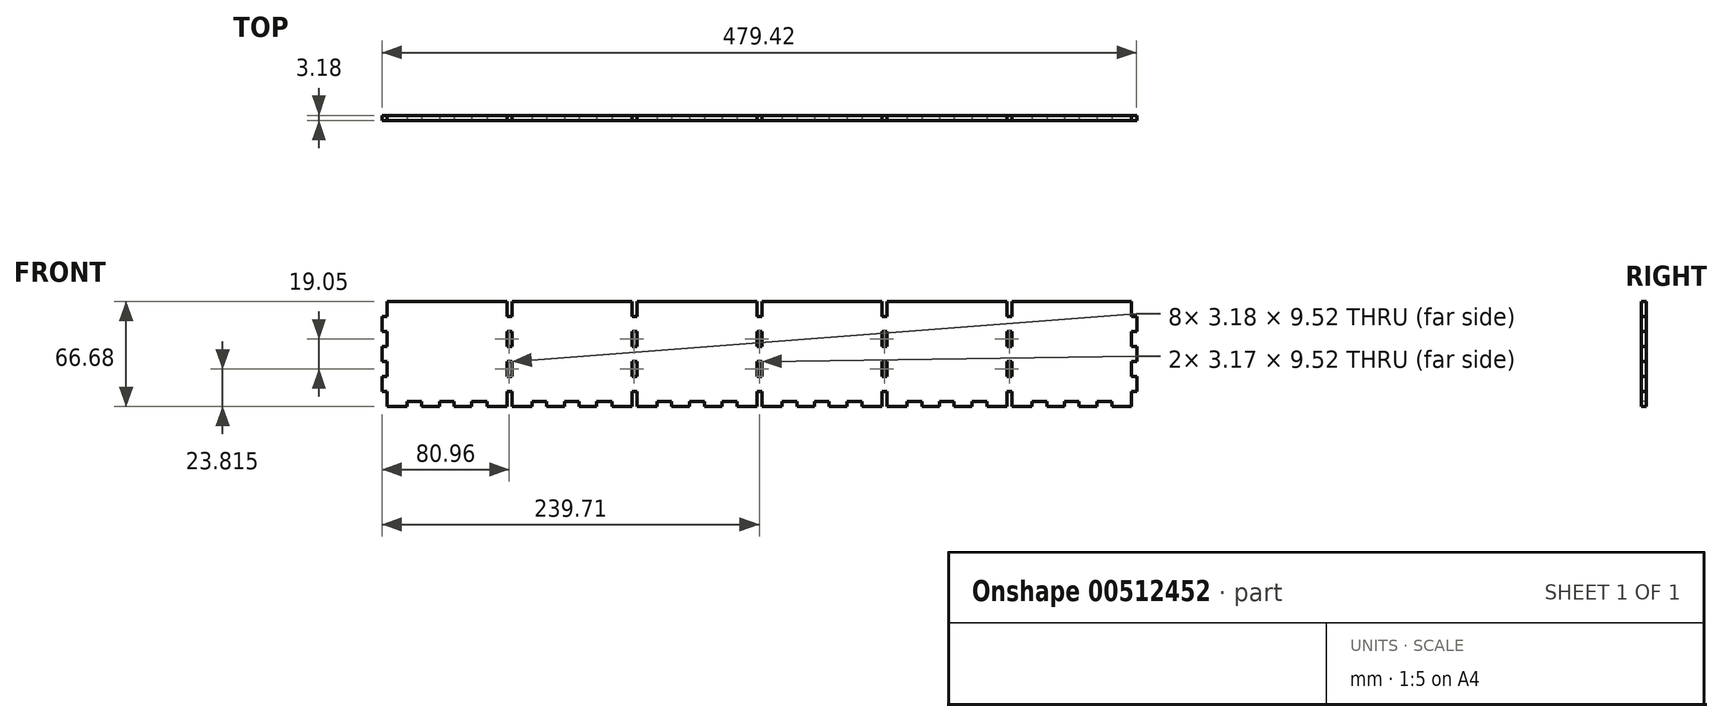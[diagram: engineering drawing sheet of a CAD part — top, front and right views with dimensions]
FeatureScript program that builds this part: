
annotation { "Feature Type Name" : "Feature", "Feature Type Description" : "" }
export const myFeature = defineFeature(function(context is Context, id is Id, definition is map)
    precondition{}
    {
        {
            var Q0;
            Q0=qCreatedBy(makeId("Front.planeOp"),FACE);
            var sketch = newSketch(context, id + "F0", { "sketchPlane" : qUnion([Q0])});
            skLineSegment(sketch, "E0.bottom", {"start": v(-239.71, 33.34) * mm, "end": v(239.71, 33.34) * mm});
            skLineSegment(sketch, "E0.top", {"start": v(-239.71, -33.34) * mm, "end": v(239.71, -33.34) * mm});
            skLineSegment(sketch, "E0.left", {"start": v(-239.71, 33.34) * mm, "end": v(-239.71, -33.34) * mm});
            skLineSegment(sketch, "E0.right", {"start": v(239.71, 33.34) * mm, "end": v(239.71, -33.34) * mm});
            skSolve(sketch);
        }
        {
            var Q0;
            Q0=makeQuery(id+"F0.imprint","IMPRINT",FACE,{"disambiguationData":[TD([[makeQuery(id+"F0.imprint","IMPRINT",EDGE,{"derivedFrom":sQuery(id+"F0.wireOp",EDGE,"E0.bottom")}),-1.0]])]});
            extrude(context, id + "F1", {"entities" : qUnion([Q0]), "depth" : 3.17 * mm});
        }
        {
            var Q0;
            Q0=makeQuery(id+"F1.opExtrude","CAP_FACE",FACE,{"disambiguationData":[OSD([sQuery(id+"F0.wireOp",EDGE,"E0.bottom"),sQuery(id+"F0.wireOp",EDGE,"E0.top"),sQuery(id+"F0.wireOp",EDGE,"E0.left"),sQuery(id+"F0.wireOp",EDGE,"E0.right")])],"isStart":false});
            var sketch = newSketch(context, id + "F2", { "sketchPlane" : qUnion([Q0])});
            skLineSegment(sketch, "E1.bottom", {"start": v(-239.71, -33.34) * mm, "end": v(-236.54, -33.34) * mm});
            skLineSegment(sketch, "E1.top", {"start": v(-239.71, -23.81) * mm, "end": v(-236.54, -23.81) * mm});
            skLineSegment(sketch, "E1.left", {"start": v(-239.71, -33.34) * mm, "end": v(-239.71, -23.81) * mm});
            skLineSegment(sketch, "E1.right", {"start": v(-236.54, -33.34) * mm, "end": v(-236.54, -23.81) * mm});
            skLineSegment(sketch, "E2.0.1.0", {"start": v(-236.54, -14.29) * mm, "end": v(-236.54, -4.76) * mm});
            skLineSegment(sketch, "E2.0.1.1", {"start": v(-239.71, -14.29) * mm, "end": v(-239.71, -4.76) * mm});
            skLineSegment(sketch, "E2.0.1.2", {"start": v(-239.71, -4.76) * mm, "end": v(-236.54, -4.76) * mm});
            skLineSegment(sketch, "E2.0.1.3", {"start": v(-239.71, -14.29) * mm, "end": v(-236.54, -14.29) * mm});
            skLineSegment(sketch, "E2.0.2.0", {"start": v(-236.54, 4.76) * mm, "end": v(-236.54, 14.29) * mm});
            skLineSegment(sketch, "E2.0.2.1", {"start": v(-239.71, 4.76) * mm, "end": v(-239.71, 14.29) * mm});
            skLineSegment(sketch, "E2.0.2.2", {"start": v(-239.71, 14.29) * mm, "end": v(-236.54, 14.29) * mm});
            skLineSegment(sketch, "E2.0.2.3", {"start": v(-239.71, 4.76) * mm, "end": v(-236.54, 4.76) * mm});
            skLineSegment(sketch, "E2.0.3.0", {"start": v(-236.54, 23.81) * mm, "end": v(-236.54, 33.34) * mm});
            skLineSegment(sketch, "E2.0.3.1", {"start": v(-239.71, 23.81) * mm, "end": v(-239.71, 33.34) * mm});
            skLineSegment(sketch, "E2.0.3.2", {"start": v(-239.71, 33.34) * mm, "end": v(-236.54, 33.34) * mm});
            skLineSegment(sketch, "E2.0.3.3", {"start": v(-239.71, 23.81) * mm, "end": v(-236.54, 23.81) * mm});
            skLineSegment(sketch, "E2.1.0.0", {"start": v(-157.16, -33.34) * mm, "end": v(-157.16, -23.81) * mm});
            skLineSegment(sketch, "E2.1.0.1", {"start": v(-160.34, -33.34) * mm, "end": v(-160.34, -23.81) * mm});
            skLineSegment(sketch, "E2.1.0.2", {"start": v(-160.34, -23.81) * mm, "end": v(-157.16, -23.81) * mm});
            skLineSegment(sketch, "E2.1.0.3", {"start": v(-160.34, -33.34) * mm, "end": v(-157.16, -33.34) * mm});
            skLineSegment(sketch, "E2.1.1.0", {"start": v(-157.16, -14.29) * mm, "end": v(-157.16, -4.76) * mm});
            skLineSegment(sketch, "E2.1.1.1", {"start": v(-160.34, -14.29) * mm, "end": v(-160.34, -4.76) * mm});
            skLineSegment(sketch, "E2.1.1.2", {"start": v(-160.34, -4.76) * mm, "end": v(-157.16, -4.76) * mm});
            skLineSegment(sketch, "E2.1.1.3", {"start": v(-160.34, -14.29) * mm, "end": v(-157.16, -14.29) * mm});
            skLineSegment(sketch, "E2.1.2.0", {"start": v(-157.16, 4.76) * mm, "end": v(-157.16, 14.29) * mm});
            skLineSegment(sketch, "E2.1.2.1", {"start": v(-160.34, 4.76) * mm, "end": v(-160.34, 14.29) * mm});
            skLineSegment(sketch, "E2.1.2.2", {"start": v(-160.34, 14.29) * mm, "end": v(-157.16, 14.29) * mm});
            skLineSegment(sketch, "E2.1.2.3", {"start": v(-160.34, 4.76) * mm, "end": v(-157.16, 4.76) * mm});
            skLineSegment(sketch, "E2.1.3.0", {"start": v(-157.16, 23.81) * mm, "end": v(-157.16, 33.34) * mm});
            skLineSegment(sketch, "E2.1.3.1", {"start": v(-160.34, 23.81) * mm, "end": v(-160.34, 33.34) * mm});
            skLineSegment(sketch, "E2.1.3.2", {"start": v(-160.34, 33.34) * mm, "end": v(-157.16, 33.34) * mm});
            skLineSegment(sketch, "E2.1.3.3", {"start": v(-160.34, 23.81) * mm, "end": v(-157.16, 23.81) * mm});
            skLineSegment(sketch, "E2.2.0.0", {"start": v(-77.79, -33.34) * mm, "end": v(-77.79, -23.81) * mm});
            skLineSegment(sketch, "E2.2.0.1", {"start": v(-80.96, -33.34) * mm, "end": v(-80.96, -23.81) * mm});
            skLineSegment(sketch, "E2.2.0.2", {"start": v(-80.96, -23.81) * mm, "end": v(-77.79, -23.81) * mm});
            skLineSegment(sketch, "E2.2.0.3", {"start": v(-80.96, -33.34) * mm, "end": v(-77.79, -33.34) * mm});
            skLineSegment(sketch, "E2.2.1.0", {"start": v(-77.79, -14.29) * mm, "end": v(-77.79, -4.76) * mm});
            skLineSegment(sketch, "E2.2.1.1", {"start": v(-80.96, -14.29) * mm, "end": v(-80.96, -4.76) * mm});
            skLineSegment(sketch, "E2.2.1.2", {"start": v(-80.96, -4.76) * mm, "end": v(-77.79, -4.76) * mm});
            skLineSegment(sketch, "E2.2.1.3", {"start": v(-80.96, -14.29) * mm, "end": v(-77.79, -14.29) * mm});
            skLineSegment(sketch, "E2.2.2.0", {"start": v(-77.79, 4.76) * mm, "end": v(-77.79, 14.29) * mm});
            skLineSegment(sketch, "E2.2.2.1", {"start": v(-80.96, 4.76) * mm, "end": v(-80.96, 14.29) * mm});
            skLineSegment(sketch, "E2.2.2.2", {"start": v(-80.96, 14.29) * mm, "end": v(-77.79, 14.29) * mm});
            skLineSegment(sketch, "E2.2.2.3", {"start": v(-80.96, 4.76) * mm, "end": v(-77.79, 4.76) * mm});
            skLineSegment(sketch, "E2.2.3.0", {"start": v(-77.79, 23.81) * mm, "end": v(-77.79, 33.34) * mm});
            skLineSegment(sketch, "E2.2.3.1", {"start": v(-80.96, 23.81) * mm, "end": v(-80.96, 33.34) * mm});
            skLineSegment(sketch, "E2.2.3.2", {"start": v(-80.96, 33.34) * mm, "end": v(-77.79, 33.34) * mm});
            skLineSegment(sketch, "E2.2.3.3", {"start": v(-80.96, 23.81) * mm, "end": v(-77.79, 23.81) * mm});
            skLineSegment(sketch, "E2.direction1", {"start": v(-239.71, -33.34) * mm, "end": v(-160.34, -33.34) * mm, "construction": true});
            skLineSegment(sketch, "E2.direction2", {"start": v(-239.71, -33.34) * mm, "end": v(-239.71, -14.29) * mm, "construction": true});
            skLineSegment(sketch, "E3.0.3.0", {"start": v(1.59, -33.34) * mm, "end": v(1.59, -23.81) * mm});
            skLineSegment(sketch, "E3.3.3.0", {"start": v(-1.59, -33.34) * mm, "end": v(-1.59, -23.81) * mm});
            skLineSegment(sketch, "E3.6.3.0", {"start": v(-1.59, -23.81) * mm, "end": v(1.59, -23.81) * mm});
            skLineSegment(sketch, "E3.9.3.0", {"start": v(-1.59, -33.34) * mm, "end": v(1.59, -33.34) * mm});
            skLineSegment(sketch, "E3.0.3.1", {"start": v(1.59, -14.29) * mm, "end": v(1.59, -4.76) * mm});
            skLineSegment(sketch, "E3.3.3.1", {"start": v(-1.59, -14.29) * mm, "end": v(-1.59, -4.76) * mm});
            skLineSegment(sketch, "E3.6.3.1", {"start": v(-1.59, -4.76) * mm, "end": v(1.59, -4.76) * mm});
            skLineSegment(sketch, "E3.9.3.1", {"start": v(-1.59, -14.29) * mm, "end": v(1.59, -14.29) * mm});
            skLineSegment(sketch, "E3.0.3.2", {"start": v(1.59, 4.76) * mm, "end": v(1.59, 14.29) * mm});
            skLineSegment(sketch, "E3.3.3.2", {"start": v(-1.59, 4.76) * mm, "end": v(-1.59, 14.29) * mm});
            skLineSegment(sketch, "E3.6.3.2", {"start": v(-1.59, 14.29) * mm, "end": v(1.59, 14.29) * mm});
            skLineSegment(sketch, "E3.9.3.2", {"start": v(-1.59, 4.76) * mm, "end": v(1.59, 4.76) * mm});
            skLineSegment(sketch, "E3.0.3.3", {"start": v(1.59, 23.81) * mm, "end": v(1.59, 33.34) * mm});
            skLineSegment(sketch, "E3.3.3.3", {"start": v(-1.59, 23.81) * mm, "end": v(-1.59, 33.34) * mm});
            skLineSegment(sketch, "E3.6.3.3", {"start": v(-1.59, 33.34) * mm, "end": v(1.59, 33.34) * mm});
            skLineSegment(sketch, "E3.9.3.3", {"start": v(-1.59, 23.81) * mm, "end": v(1.59, 23.81) * mm});
            skLineSegment(sketch, "E3.0.4.0", {"start": v(80.96, -33.34) * mm, "end": v(80.96, -23.81) * mm});
            skLineSegment(sketch, "E3.3.4.0", {"start": v(77.79, -33.34) * mm, "end": v(77.79, -23.81) * mm});
            skLineSegment(sketch, "E3.6.4.0", {"start": v(77.79, -23.81) * mm, "end": v(80.96, -23.81) * mm});
            skLineSegment(sketch, "E3.9.4.0", {"start": v(77.79, -33.34) * mm, "end": v(80.96, -33.34) * mm});
            skLineSegment(sketch, "E3.0.4.1", {"start": v(80.96, -14.29) * mm, "end": v(80.96, -4.76) * mm});
            skLineSegment(sketch, "E3.3.4.1", {"start": v(77.79, -14.29) * mm, "end": v(77.79, -4.76) * mm});
            skLineSegment(sketch, "E3.6.4.1", {"start": v(77.79, -4.76) * mm, "end": v(80.96, -4.76) * mm});
            skLineSegment(sketch, "E3.9.4.1", {"start": v(77.79, -14.29) * mm, "end": v(80.96, -14.29) * mm});
            skLineSegment(sketch, "E3.0.4.2", {"start": v(80.96, 4.76) * mm, "end": v(80.96, 14.29) * mm});
            skLineSegment(sketch, "E3.3.4.2", {"start": v(77.79, 4.76) * mm, "end": v(77.79, 14.29) * mm});
            skLineSegment(sketch, "E3.6.4.2", {"start": v(77.79, 14.29) * mm, "end": v(80.96, 14.29) * mm});
            skLineSegment(sketch, "E3.9.4.2", {"start": v(77.79, 4.76) * mm, "end": v(80.96, 4.76) * mm});
            skLineSegment(sketch, "E3.0.4.3", {"start": v(80.96, 23.81) * mm, "end": v(80.96, 33.34) * mm});
            skLineSegment(sketch, "E3.3.4.3", {"start": v(77.79, 23.81) * mm, "end": v(77.79, 33.34) * mm});
            skLineSegment(sketch, "E3.6.4.3", {"start": v(77.79, 33.34) * mm, "end": v(80.96, 33.34) * mm});
            skLineSegment(sketch, "E3.9.4.3", {"start": v(77.79, 23.81) * mm, "end": v(80.96, 23.81) * mm});
            skLineSegment(sketch, "E3.0.5.0", {"start": v(160.34, -33.34) * mm, "end": v(160.34, -23.81) * mm});
            skLineSegment(sketch, "E3.3.5.0", {"start": v(157.16, -33.34) * mm, "end": v(157.16, -23.81) * mm});
            skLineSegment(sketch, "E3.6.5.0", {"start": v(157.16, -23.81) * mm, "end": v(160.34, -23.81) * mm});
            skLineSegment(sketch, "E3.9.5.0", {"start": v(157.16, -33.34) * mm, "end": v(160.34, -33.34) * mm});
            skLineSegment(sketch, "E3.0.5.1", {"start": v(160.34, -14.29) * mm, "end": v(160.34, -4.76) * mm});
            skLineSegment(sketch, "E3.3.5.1", {"start": v(157.16, -14.29) * mm, "end": v(157.16, -4.76) * mm});
            skLineSegment(sketch, "E3.6.5.1", {"start": v(157.16, -4.76) * mm, "end": v(160.34, -4.76) * mm});
            skLineSegment(sketch, "E3.9.5.1", {"start": v(157.16, -14.29) * mm, "end": v(160.34, -14.29) * mm});
            skLineSegment(sketch, "E3.0.5.2", {"start": v(160.34, 4.76) * mm, "end": v(160.34, 14.29) * mm});
            skLineSegment(sketch, "E3.3.5.2", {"start": v(157.16, 4.76) * mm, "end": v(157.16, 14.29) * mm});
            skLineSegment(sketch, "E3.6.5.2", {"start": v(157.16, 14.29) * mm, "end": v(160.34, 14.29) * mm});
            skLineSegment(sketch, "E3.9.5.2", {"start": v(157.16, 4.76) * mm, "end": v(160.34, 4.76) * mm});
            skLineSegment(sketch, "E3.0.5.3", {"start": v(160.34, 23.81) * mm, "end": v(160.34, 33.34) * mm});
            skLineSegment(sketch, "E3.3.5.3", {"start": v(157.16, 23.81) * mm, "end": v(157.16, 33.34) * mm});
            skLineSegment(sketch, "E3.6.5.3", {"start": v(157.16, 33.34) * mm, "end": v(160.34, 33.34) * mm});
            skLineSegment(sketch, "E3.9.5.3", {"start": v(157.16, 23.81) * mm, "end": v(160.34, 23.81) * mm});
            skLineSegment(sketch, "E3.0.6.0", {"start": v(239.71, -33.34) * mm, "end": v(239.71, -23.81) * mm});
            skLineSegment(sketch, "E3.3.6.0", {"start": v(236.54, -33.34) * mm, "end": v(236.54, -23.81) * mm});
            skLineSegment(sketch, "E3.6.6.0", {"start": v(236.54, -23.81) * mm, "end": v(239.71, -23.81) * mm});
            skLineSegment(sketch, "E3.9.6.0", {"start": v(236.54, -33.34) * mm, "end": v(239.71, -33.34) * mm});
            skLineSegment(sketch, "E3.0.6.1", {"start": v(239.71, -14.29) * mm, "end": v(239.71, -4.76) * mm});
            skLineSegment(sketch, "E3.3.6.1", {"start": v(236.54, -14.29) * mm, "end": v(236.54, -4.76) * mm});
            skLineSegment(sketch, "E3.6.6.1", {"start": v(236.54, -4.76) * mm, "end": v(239.71, -4.76) * mm});
            skLineSegment(sketch, "E3.9.6.1", {"start": v(236.54, -14.29) * mm, "end": v(239.71, -14.29) * mm});
            skLineSegment(sketch, "E3.0.6.2", {"start": v(239.71, 4.76) * mm, "end": v(239.71, 14.29) * mm});
            skLineSegment(sketch, "E3.3.6.2", {"start": v(236.54, 4.76) * mm, "end": v(236.54, 14.29) * mm});
            skLineSegment(sketch, "E3.6.6.2", {"start": v(236.54, 14.29) * mm, "end": v(239.71, 14.29) * mm});
            skLineSegment(sketch, "E3.9.6.2", {"start": v(236.54, 4.76) * mm, "end": v(239.71, 4.76) * mm});
            skLineSegment(sketch, "E3.0.6.3", {"start": v(239.71, 23.81) * mm, "end": v(239.71, 33.34) * mm});
            skLineSegment(sketch, "E3.3.6.3", {"start": v(236.54, 23.81) * mm, "end": v(236.54, 33.34) * mm});
            skLineSegment(sketch, "E3.6.6.3", {"start": v(236.54, 33.34) * mm, "end": v(239.71, 33.34) * mm});
            skLineSegment(sketch, "E3.9.6.3", {"start": v(236.54, 23.81) * mm, "end": v(239.71, 23.81) * mm});
            skSolve(sketch);
        }
        {
            var Q0;
            Q0 = qSketchRegion(id + "F2", true);
            extrude(context, id + "F3", {"entities" : qUnion([Q0]), "operationType" : NewBodyOperationType.REMOVE, "endBound" : BoundingType.THROUGH_ALL, "oppositeDirection" : true, "depth" : 25.4 * mm});
        }
        {
            var Q0;
            Q0=makeQuery(id+"F1.opExtrude","CAP_FACE",FACE,{"disambiguationData":[OSD([sQuery(id+"F0.wireOp",EDGE,"E0.bottom"),sQuery(id+"F0.wireOp",EDGE,"E0.top"),sQuery(id+"F0.wireOp",EDGE,"E0.left"),sQuery(id+"F0.wireOp",EDGE,"E0.right")])],"isStart":false});
            var sketch = newSketch(context, id + "F4", { "sketchPlane" : qUnion([Q0])});
            skLineSegment(sketch, "E4.bottom", {"start": v(-223.84, -33.34) * mm, "end": v(-214.31, -33.34) * mm});
            skLineSegment(sketch, "E4.top", {"start": v(-223.84, -30.16) * mm, "end": v(-214.31, -30.16) * mm});
            skLineSegment(sketch, "E4.left", {"start": v(-223.84, -33.34) * mm, "end": v(-223.84, -30.16) * mm});
            skLineSegment(sketch, "E4.right", {"start": v(-214.31, -33.34) * mm, "end": v(-214.31, -30.16) * mm});
            skLineSegment(sketch, "E5.1.0.0", {"start": v(-193.68, -33.34) * mm, "end": v(-193.68, -30.16) * mm});
            skLineSegment(sketch, "E5.1.0.1", {"start": v(-203.2, -33.34) * mm, "end": v(-203.2, -30.16) * mm});
            skLineSegment(sketch, "E5.1.0.2", {"start": v(-203.2, -30.16) * mm, "end": v(-193.68, -30.16) * mm});
            skLineSegment(sketch, "E5.1.0.3", {"start": v(-203.2, -33.34) * mm, "end": v(-193.68, -33.34) * mm});
            skLineSegment(sketch, "E5.2.0.0", {"start": v(-173.04, -33.34) * mm, "end": v(-173.04, -30.16) * mm});
            skLineSegment(sketch, "E5.2.0.1", {"start": v(-182.56, -33.34) * mm, "end": v(-182.56, -30.16) * mm});
            skLineSegment(sketch, "E5.2.0.2", {"start": v(-182.56, -30.16) * mm, "end": v(-173.04, -30.16) * mm});
            skLineSegment(sketch, "E5.2.0.3", {"start": v(-182.56, -33.34) * mm, "end": v(-173.04, -33.34) * mm});
            skLineSegment(sketch, "E5.direction1", {"start": v(-223.84, -33.34) * mm, "end": v(-203.2, -33.34) * mm, "construction": true});
            skLineSegment(sketch, "E6.1.0.0", {"start": v(-144.46, -30.16) * mm, "end": v(-134.94, -30.16) * mm});
            skLineSegment(sketch, "E6.1.0.1", {"start": v(-144.46, -33.34) * mm, "end": v(-123.83, -33.34) * mm, "construction": true});
            skLineSegment(sketch, "E6.1.0.2", {"start": v(-123.83, -33.34) * mm, "end": v(-114.3, -33.34) * mm});
            skLineSegment(sketch, "E6.1.0.3", {"start": v(-103.19, -33.34) * mm, "end": v(-93.66, -33.34) * mm});
            skLineSegment(sketch, "E6.1.0.4", {"start": v(-123.83, -30.16) * mm, "end": v(-114.3, -30.16) * mm});
            skLineSegment(sketch, "E6.1.0.5", {"start": v(-103.19, -30.16) * mm, "end": v(-93.66, -30.16) * mm});
            skLineSegment(sketch, "E6.1.0.6", {"start": v(-144.46, -33.34) * mm, "end": v(-134.94, -33.34) * mm});
            skLineSegment(sketch, "E6.1.0.7", {"start": v(-134.94, -33.34) * mm, "end": v(-134.94, -30.16) * mm});
            skLineSegment(sketch, "E6.1.0.8", {"start": v(-144.46, -33.34) * mm, "end": v(-144.46, -30.16) * mm});
            skLineSegment(sketch, "E6.1.0.9", {"start": v(-103.19, -33.34) * mm, "end": v(-103.19, -30.16) * mm});
            skLineSegment(sketch, "E6.1.0.10", {"start": v(-123.83, -33.34) * mm, "end": v(-123.83, -30.16) * mm});
            skLineSegment(sketch, "E6.1.0.11", {"start": v(-93.66, -33.34) * mm, "end": v(-93.66, -30.16) * mm});
            skLineSegment(sketch, "E6.1.0.12", {"start": v(-114.3, -33.34) * mm, "end": v(-114.3, -30.16) * mm});
            skLineSegment(sketch, "E6.2.0.0", {"start": v(-65.09, -30.16) * mm, "end": v(-55.56, -30.16) * mm});
            skLineSegment(sketch, "E6.2.0.1", {"start": v(-65.09, -33.34) * mm, "end": v(-44.45, -33.34) * mm, "construction": true});
            skLineSegment(sketch, "E6.2.0.2", {"start": v(-44.45, -33.34) * mm, "end": v(-34.93, -33.34) * mm});
            skLineSegment(sketch, "E6.2.0.3", {"start": v(-23.81, -33.34) * mm, "end": v(-14.29, -33.34) * mm});
            skLineSegment(sketch, "E6.2.0.4", {"start": v(-44.45, -30.16) * mm, "end": v(-34.93, -30.16) * mm});
            skLineSegment(sketch, "E6.2.0.5", {"start": v(-23.81, -30.16) * mm, "end": v(-14.29, -30.16) * mm});
            skLineSegment(sketch, "E6.2.0.6", {"start": v(-65.09, -33.34) * mm, "end": v(-55.56, -33.34) * mm});
            skLineSegment(sketch, "E6.2.0.7", {"start": v(-55.56, -33.34) * mm, "end": v(-55.56, -30.16) * mm});
            skLineSegment(sketch, "E6.2.0.8", {"start": v(-65.09, -33.34) * mm, "end": v(-65.09, -30.16) * mm});
            skLineSegment(sketch, "E6.2.0.9", {"start": v(-23.81, -33.34) * mm, "end": v(-23.81, -30.16) * mm});
            skLineSegment(sketch, "E6.2.0.10", {"start": v(-44.45, -33.34) * mm, "end": v(-44.45, -30.16) * mm});
            skLineSegment(sketch, "E6.2.0.11", {"start": v(-14.29, -33.34) * mm, "end": v(-14.29, -30.16) * mm});
            skLineSegment(sketch, "E6.2.0.12", {"start": v(-34.93, -33.34) * mm, "end": v(-34.93, -30.16) * mm});
            skLineSegment(sketch, "E6.3.0.0", {"start": v(14.29, -30.16) * mm, "end": v(23.81, -30.16) * mm});
            skLineSegment(sketch, "E6.3.0.1", {"start": v(14.29, -33.34) * mm, "end": v(34.92, -33.34) * mm, "construction": true});
            skLineSegment(sketch, "E6.3.0.2", {"start": v(34.92, -33.34) * mm, "end": v(44.45, -33.34) * mm});
            skLineSegment(sketch, "E6.3.0.3", {"start": v(55.56, -33.34) * mm, "end": v(65.09, -33.34) * mm});
            skLineSegment(sketch, "E6.3.0.4", {"start": v(34.92, -30.16) * mm, "end": v(44.45, -30.16) * mm});
            skLineSegment(sketch, "E6.3.0.5", {"start": v(55.56, -30.16) * mm, "end": v(65.09, -30.16) * mm});
            skLineSegment(sketch, "E6.3.0.6", {"start": v(14.29, -33.34) * mm, "end": v(23.81, -33.34) * mm});
            skLineSegment(sketch, "E6.3.0.7", {"start": v(23.81, -33.34) * mm, "end": v(23.81, -30.16) * mm});
            skLineSegment(sketch, "E6.3.0.8", {"start": v(14.29, -33.34) * mm, "end": v(14.29, -30.16) * mm});
            skLineSegment(sketch, "E6.3.0.9", {"start": v(55.56, -33.34) * mm, "end": v(55.56, -30.16) * mm});
            skLineSegment(sketch, "E6.3.0.10", {"start": v(34.92, -33.34) * mm, "end": v(34.92, -30.16) * mm});
            skLineSegment(sketch, "E6.3.0.11", {"start": v(65.09, -33.34) * mm, "end": v(65.09, -30.16) * mm});
            skLineSegment(sketch, "E6.3.0.12", {"start": v(44.45, -33.34) * mm, "end": v(44.45, -30.16) * mm});
            skLineSegment(sketch, "E6.4.0.0", {"start": v(93.66, -30.16) * mm, "end": v(103.19, -30.16) * mm});
            skLineSegment(sketch, "E6.4.0.1", {"start": v(93.66, -33.34) * mm, "end": v(114.3, -33.34) * mm, "construction": true});
            skLineSegment(sketch, "E6.4.0.2", {"start": v(114.3, -33.34) * mm, "end": v(123.82, -33.34) * mm});
            skLineSegment(sketch, "E6.4.0.3", {"start": v(134.94, -33.34) * mm, "end": v(144.46, -33.34) * mm});
            skLineSegment(sketch, "E6.4.0.4", {"start": v(114.3, -30.16) * mm, "end": v(123.82, -30.16) * mm});
            skLineSegment(sketch, "E6.4.0.5", {"start": v(134.94, -30.16) * mm, "end": v(144.46, -30.16) * mm});
            skLineSegment(sketch, "E6.4.0.6", {"start": v(93.66, -33.34) * mm, "end": v(103.19, -33.34) * mm});
            skLineSegment(sketch, "E6.4.0.7", {"start": v(103.19, -33.34) * mm, "end": v(103.19, -30.16) * mm});
            skLineSegment(sketch, "E6.4.0.8", {"start": v(93.66, -33.34) * mm, "end": v(93.66, -30.16) * mm});
            skLineSegment(sketch, "E6.4.0.9", {"start": v(134.94, -33.34) * mm, "end": v(134.94, -30.16) * mm});
            skLineSegment(sketch, "E6.4.0.10", {"start": v(114.3, -33.34) * mm, "end": v(114.3, -30.16) * mm});
            skLineSegment(sketch, "E6.4.0.11", {"start": v(144.46, -33.34) * mm, "end": v(144.46, -30.16) * mm});
            skLineSegment(sketch, "E6.4.0.12", {"start": v(123.82, -33.34) * mm, "end": v(123.82, -30.16) * mm});
            skLineSegment(sketch, "E6.5.0.0", {"start": v(173.04, -30.16) * mm, "end": v(182.56, -30.16) * mm});
            skLineSegment(sketch, "E6.5.0.1", {"start": v(173.04, -33.34) * mm, "end": v(193.67, -33.34) * mm, "construction": true});
            skLineSegment(sketch, "E6.5.0.2", {"start": v(193.67, -33.34) * mm, "end": v(203.2, -33.34) * mm});
            skLineSegment(sketch, "E6.5.0.3", {"start": v(214.31, -33.34) * mm, "end": v(223.84, -33.34) * mm});
            skLineSegment(sketch, "E6.5.0.4", {"start": v(193.67, -30.16) * mm, "end": v(203.2, -30.16) * mm});
            skLineSegment(sketch, "E6.5.0.5", {"start": v(214.31, -30.16) * mm, "end": v(223.84, -30.16) * mm});
            skLineSegment(sketch, "E6.5.0.6", {"start": v(173.04, -33.34) * mm, "end": v(182.56, -33.34) * mm});
            skLineSegment(sketch, "E6.5.0.7", {"start": v(182.56, -33.34) * mm, "end": v(182.56, -30.16) * mm});
            skLineSegment(sketch, "E6.5.0.8", {"start": v(173.04, -33.34) * mm, "end": v(173.04, -30.16) * mm});
            skLineSegment(sketch, "E6.5.0.9", {"start": v(214.31, -33.34) * mm, "end": v(214.31, -30.16) * mm});
            skLineSegment(sketch, "E6.5.0.10", {"start": v(193.67, -33.34) * mm, "end": v(193.67, -30.16) * mm});
            skLineSegment(sketch, "E6.5.0.11", {"start": v(223.84, -33.34) * mm, "end": v(223.84, -30.16) * mm});
            skLineSegment(sketch, "E6.5.0.12", {"start": v(203.2, -33.34) * mm, "end": v(203.2, -30.16) * mm});
            skLineSegment(sketch, "E6.direction1", {"start": v(-223.84, -33.34) * mm, "end": v(-144.46, -33.34) * mm, "construction": true});
            skSolve(sketch);
        }
        {
            var Q0;
            Q0 = qSketchRegion(id + "F4", true);
            extrude(context, id + "F5", {"entities" : qUnion([Q0]), "operationType" : NewBodyOperationType.REMOVE, "endBound" : BoundingType.THROUGH_ALL, "oppositeDirection" : true, "depth" : 25.4 * mm});
        }
    });
